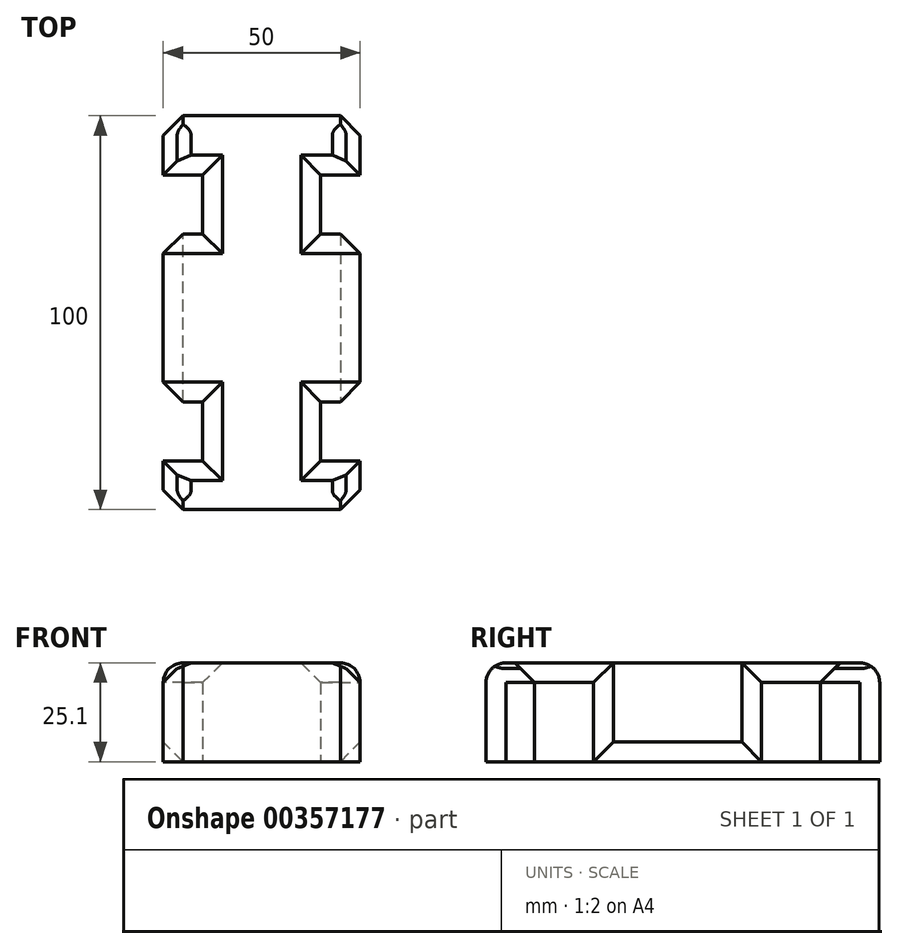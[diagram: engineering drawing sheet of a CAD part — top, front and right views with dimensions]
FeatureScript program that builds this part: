
annotation { "Feature Type Name" : "Feature", "Feature Type Description" : "" }
export const myFeature = defineFeature(function(context is Context, id is Id, definition is map)
    precondition{}
    {
        {
            var Q0;
            Q0=qCreatedBy(makeId("Top.planeOp"),FACE);
            var sketch = newSketch(context, id + "F0", { "sketchPlane" : qUnion([Q0])});
            skLineSegment(sketch, "E0.bottom", {"start": v(-25, 50) * mm, "end": v(25, 50) * mm});
            skLineSegment(sketch, "E0.top", {"start": v(-25, -50) * mm, "end": v(25, -50) * mm});
            skLineSegment(sketch, "E0.left", {"start": v(-25, 50) * mm, "end": v(-25, 35) * mm});
            skLineSegment(sketch, "E0.right", {"start": v(25, 50) * mm, "end": v(25, 35) * mm});
            skPoint(sketch, "E0.middle", {"position": v(0, 0) * mm});
            skLineSegment(sketch, "E1.bottom", {"start": v(-25, 35) * mm, "end": v(-15, 35) * mm});
            skLineSegment(sketch, "E1.top", {"start": v(-25, 20) * mm, "end": v(-15, 20) * mm});
            skLineSegment(sketch, "E1.right", {"start": v(-15, 35) * mm, "end": v(-15, 20) * mm});
            skLineSegment(sketch, "E2.trimOffspring", {"start": v(-25, 20) * mm, "end": v(-25, -22.68) * mm});
            skLineSegment(sketch, "E3.bottom", {"start": v(25, 20) * mm, "end": v(15, 20) * mm});
            skLineSegment(sketch, "E3.top", {"start": v(25, 35) * mm, "end": v(15, 35) * mm});
            skLineSegment(sketch, "E3.right", {"start": v(15, 20) * mm, "end": v(15, 35) * mm});
            skLineSegment(sketch, "E4.trimOffspring", {"start": v(25, 20) * mm, "end": v(25, -22.68) * mm});
            skLineSegment(sketch, "E5.bottom", {"start": v(-25, -22.68) * mm, "end": v(-15, -22.68) * mm});
            skLineSegment(sketch, "E5.top", {"start": v(-25, -37.68) * mm, "end": v(-15, -37.68) * mm});
            skLineSegment(sketch, "E5.right", {"start": v(-15, -22.68) * mm, "end": v(-15, -37.68) * mm});
            skLineSegment(sketch, "E6.trimOffspring", {"start": v(-25, -37.68) * mm, "end": v(-25, -50) * mm});
            skLineSegment(sketch, "E7.bottom", {"start": v(25, -37.68) * mm, "end": v(15, -37.68) * mm});
            skLineSegment(sketch, "E7.top", {"start": v(25, -22.68) * mm, "end": v(15, -22.68) * mm});
            skLineSegment(sketch, "E7.right", {"start": v(15, -37.68) * mm, "end": v(15, -22.68) * mm});
            skLineSegment(sketch, "E8.trimOffspring", {"start": v(25, -37.68) * mm, "end": v(25, -50) * mm});
            skSolve(sketch);
        }
        {
            var Q0;
            Q0 = qSketchRegion(id + "F0", true);
            extrude(context, id + "F1", {"entities" : qUnion([Q0]), "depth" : 25.1 * mm});
        }
        {
            var Q0;
            Q0=makeQuery(id+"F1.opExtrude","CAP_EDGE",EDGE,{"disambiguationData":[OSD([sQuery(id+"F0.wireOp",EDGE,"E4.trimOffspring")])],"isStart":false});
            var Q1;
            Q1=makeQuery(id+"F1.opExtrude","CAP_EDGE",EDGE,{"disambiguationData":[OSD([sQuery(id+"F0.wireOp",EDGE,"E2.trimOffspring")])],"isStart":false});
            var Q2;
            Q2=makeQuery(id+"F1.opExtrude","CAP_EDGE",EDGE,{"disambiguationData":[OSD([sQuery(id+"F0.wireOp",EDGE,"E0.top")])],"isStart":false});
            var Q3;
            Q3=makeQuery(id+"F1.opExtrude","CAP_EDGE",EDGE,{"disambiguationData":[OSD([sQuery(id+"F0.wireOp",EDGE,"E0.bottom")])],"isStart":false});
            fillet(context, id + "F2", {"entities" : qUnion([Q0, Q1, Q2, Q3]), "radius" : 5 * mm, "tangentPropagation" : true, "allowEdgeOverflow" : false});
        }
        {
            var Q0;
            Q0=makeQuery(id+"F1.opExtrude","CAP_EDGE",EDGE,{"disambiguationData":[OSD([sQuery(id+"F0.wireOp",EDGE,"E0.left")])],"isStart":false});
            var Q1;
            Q1=makeQuery(id+"F1.opExtrude","CAP_EDGE",EDGE,{"disambiguationData":[OSD([sQuery(id+"F0.wireOp",EDGE,"E0.right")])],"isStart":false});
            var Q2;
            Q2=makeQuery(id+"F1.opExtrude","CAP_EDGE",EDGE,{"disambiguationData":[OSD([sQuery(id+"F0.wireOp",EDGE,"E8.trimOffspring")])],"isStart":false});
            var Q3;
            Q3=makeQuery(id+"F1.opExtrude","CAP_EDGE",EDGE,{"disambiguationData":[OSD([sQuery(id+"F0.wireOp",EDGE,"E6.trimOffspring")])],"isStart":false});
            chamfer(context, id + "F3", {"entities" : qUnion([Q0, Q1, Q2, Q3]), "width" : 5 * mm, "tangentPropagation" : true});
        }
        {
            var Q0;
            Q0=makeQuery(id+"F1.opExtrude","CAP_EDGE",EDGE,{"disambiguationData":[OSD([sQuery(id+"F0.wireOp",EDGE,"E4.trimOffspring")])],"isStart":true});
            var Q1;
            Q1=makeQuery(id+"F1.opExtrude","CAP_EDGE",EDGE,{"disambiguationData":[OSD([sQuery(id+"F0.wireOp",EDGE,"E2.trimOffspring")])],"isStart":true});
            var Q2;
            Q2=makeQuery(id+"F1.opExtrude","CAP_EDGE",EDGE,{"disambiguationData":[OSD([sQuery(id+"F0.wireOp",EDGE,"E3.right")])],"isStart":false});
            var Q3;
            Q3=makeQuery(id+"F1.opExtrude","CAP_EDGE",EDGE,{"disambiguationData":[OSD([sQuery(id+"F0.wireOp",EDGE,"E1.right")])],"isStart":false});
            var Q4;
            Q4=makeQuery(id+"F1.opExtrude","CAP_FACE",FACE,{"disambiguationData":[OSD([sQuery(id+"F0.wireOp",EDGE,"E0.bottom"),sQuery(id+"F0.wireOp",EDGE,"E0.top"),sQuery(id+"F0.wireOp",EDGE,"E0.left"),sQuery(id+"F0.wireOp",EDGE,"E0.right"),sQuery(id+"F0.wireOp",EDGE,"E1.bottom"),sQuery(id+"F0.wireOp",EDGE,"E1.top"),sQuery(id+"F0.wireOp",EDGE,"E1.right"),sQuery(id+"F0.wireOp",EDGE,"E2.trimOffspring"),sQuery(id+"F0.wireOp",EDGE,"E3.bottom"),sQuery(id+"F0.wireOp",EDGE,"E3.top"),sQuery(id+"F0.wireOp",EDGE,"E3.right"),sQuery(id+"F0.wireOp",EDGE,"E4.trimOffspring"),sQuery(id+"F0.wireOp",EDGE,"E5.bottom"),sQuery(id+"F0.wireOp",EDGE,"E5.top"),sQuery(id+"F0.wireOp",EDGE,"E5.right"),sQuery(id+"F0.wireOp",EDGE,"E6.trimOffspring"),sQuery(id+"F0.wireOp",EDGE,"E7.bottom"),sQuery(id+"F0.wireOp",EDGE,"E7.top"),sQuery(id+"F0.wireOp",EDGE,"E7.right"),sQuery(id+"F0.wireOp",EDGE,"E8.trimOffspring")])],"isStart":false});
            chamfer(context, id + "F4", {"entities" : qUnion([Q0, Q1, Q2, Q3, Q4]), "width" : 5 * mm, "tangentPropagation" : true});
        }
    });
